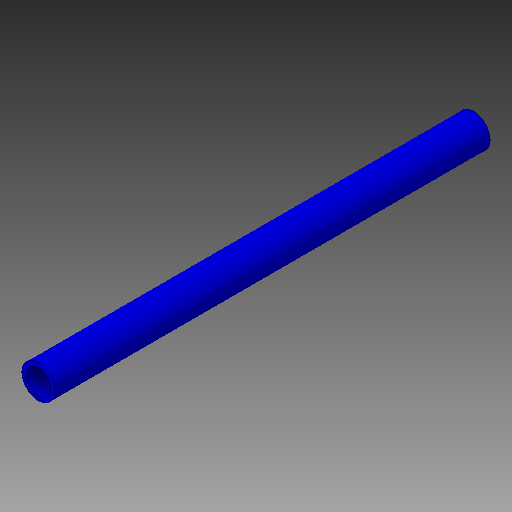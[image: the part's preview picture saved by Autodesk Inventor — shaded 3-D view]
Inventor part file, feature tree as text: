
AUTODESK INVENTOR PART (.ipt)
format: ipt  version: 2018.2 (Build 222227000, 227)  size: 105,984 bytes
history: native  units: in
note: dims shown in document units (in); Inventor stores cm internally (conversion verified against a paired STEP export)
features: extrude x1, sketch x1
ambient origin geometry x8: Origin, YZ Plane, XZ Plane, XY Plane, X Axis, Y Axis, Z Axis, Center Point
bodies: Solid1 (feature_tree)
feature tree (2):
  extrude  "Extrusion1"  Depth=17.25in
  sketch  "Sketch1"  dims[d0=1.315in d1=1.0in d2=17.25in d3=0.0in]
